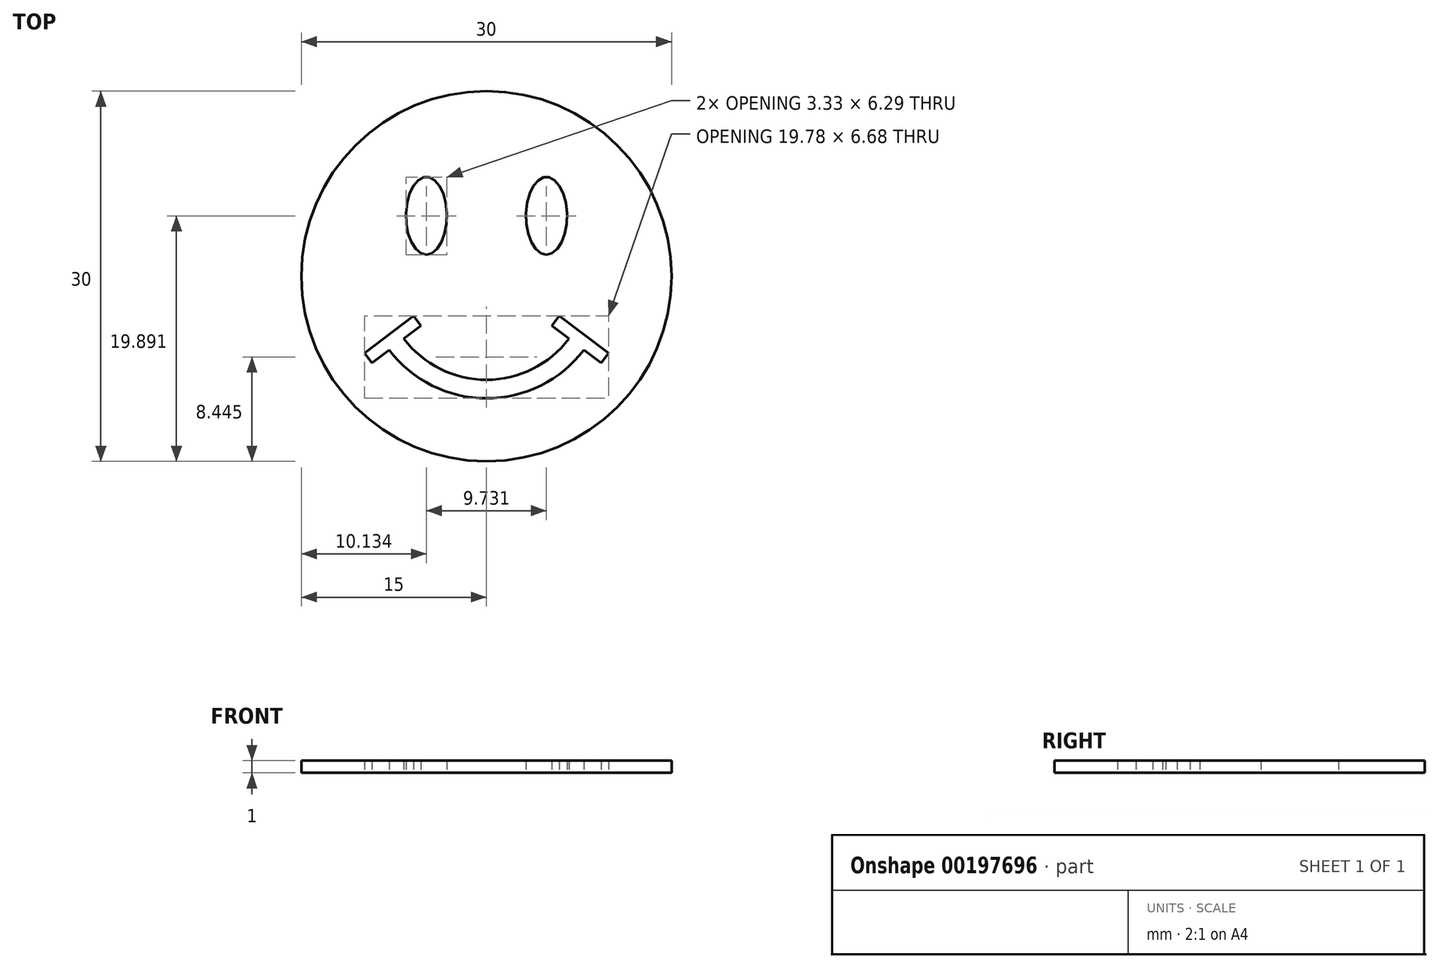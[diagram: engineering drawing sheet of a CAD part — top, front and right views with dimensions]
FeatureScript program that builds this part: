
annotation { "Feature Type Name" : "Feature", "Feature Type Description" : "" }
export const myFeature = defineFeature(function(context is Context, id is Id, definition is map)
    precondition{}
    {
        {
            var Q0;
            Q0=qCreatedBy(makeId("Top.planeOp"),FACE);
            var sketch = newSketch(context, id + "F0", { "sketchPlane" : qUnion([Q0])});
            skCircle(sketch, "E0", {"center": v(0, 0) * mm, "radius": 15 * mm});
            skLineSegment(sketch, "E1", {"start": v(0, 15) * mm, "end": v(0, -15) * mm, "construction": true});
            skArc(sketch, "E2", {"start": v(-6.7, -5.07) * mm, "mid": v(0, -8.4) * mm, "end": v(6.7, -5.07) * mm});
            skArc(sketch, "E3.0", {"start": v(-7.89, -5.97) * mm, "mid": v(0, -9.9) * mm, "end": v(7.89, -5.97) * mm});
            skLineSegment(sketch, "E4", {"start": v(-6.7, -5.07) * mm, "end": v(-5.3, -4.01) * mm});
            skLineSegment(sketch, "E5", {"start": v(-5.3, -4.01) * mm, "end": v(-5.9, -3.21) * mm});
            skLineSegment(sketch, "E6", {"start": v(-5.9, -3.21) * mm, "end": v(-9.89, -6.23) * mm});
            skLineSegment(sketch, "E7", {"start": v(-9.89, -6.23) * mm, "end": v(-9.28, -7.03) * mm});
            skLineSegment(sketch, "E8", {"start": v(-9.28, -7.03) * mm, "end": v(-7.89, -5.97) * mm});
            skLineSegment(sketch, "E9.MirrorCS", {"start": v(6.7, -5.07) * mm, "end": v(5.3, -4.01) * mm});
            skLineSegment(sketch, "E10.MirrorCS", {"start": v(5.3, -4.01) * mm, "end": v(5.9, -3.21) * mm});
            skLineSegment(sketch, "E11.MirrorCS", {"start": v(5.9, -3.21) * mm, "end": v(9.89, -6.23) * mm});
            skLineSegment(sketch, "E12.MirrorCS", {"start": v(9.89, -6.23) * mm, "end": v(9.28, -7.03) * mm});
            skLineSegment(sketch, "E13.MirrorCS", {"start": v(9.28, -7.03) * mm, "end": v(7.89, -5.97) * mm});
            skLineSegment(sketch, "E14", {"start": v(-6.7, -5.07) * mm, "end": v(-7.89, -5.97) * mm, "construction": true});
            skLineSegment(sketch, "E15", {"start": v(-7.3, -5.52) * mm, "end": v(-7.41, -5.36) * mm, "construction": true});
            skLineSegment(sketch, "E16", {"start": v(0.9, -15.1) * mm, "end": v(-6.7, -5.07) * mm, "construction": true});
            skEllipse(sketch, "E17", {"center": v(-4.87, 4.9) * mm, "majorRadius": 3.14 * mm, "minorRadius": 1.66 * mm, "majorAxis": v(0, -1)});
            skEllipse(sketch, "E18.MirrorC", {"center": v(4.87, 4.9) * mm, "majorRadius": 3.14 * mm, "minorRadius": 1.66 * mm, "majorAxis": v(0, -1)});
            skSolve(sketch);
        }
        {
            var Q0;
            Q0=makeQuery(id+"F0.imprint","IMPRINT",FACE,{"disambiguationData":[TD([[makeQuery(id+"F0.imprint","IMPRINT",EDGE,{"derivedFrom":sQuery(id+"F0.wireOp",EDGE,"E0")}),1.0]])]});
            extrude(context, id + "F1", {"entities" : qUnion([Q0]), "depth" : 1 * mm, "offsetDistance" : 25 * mm});
        }
    });
